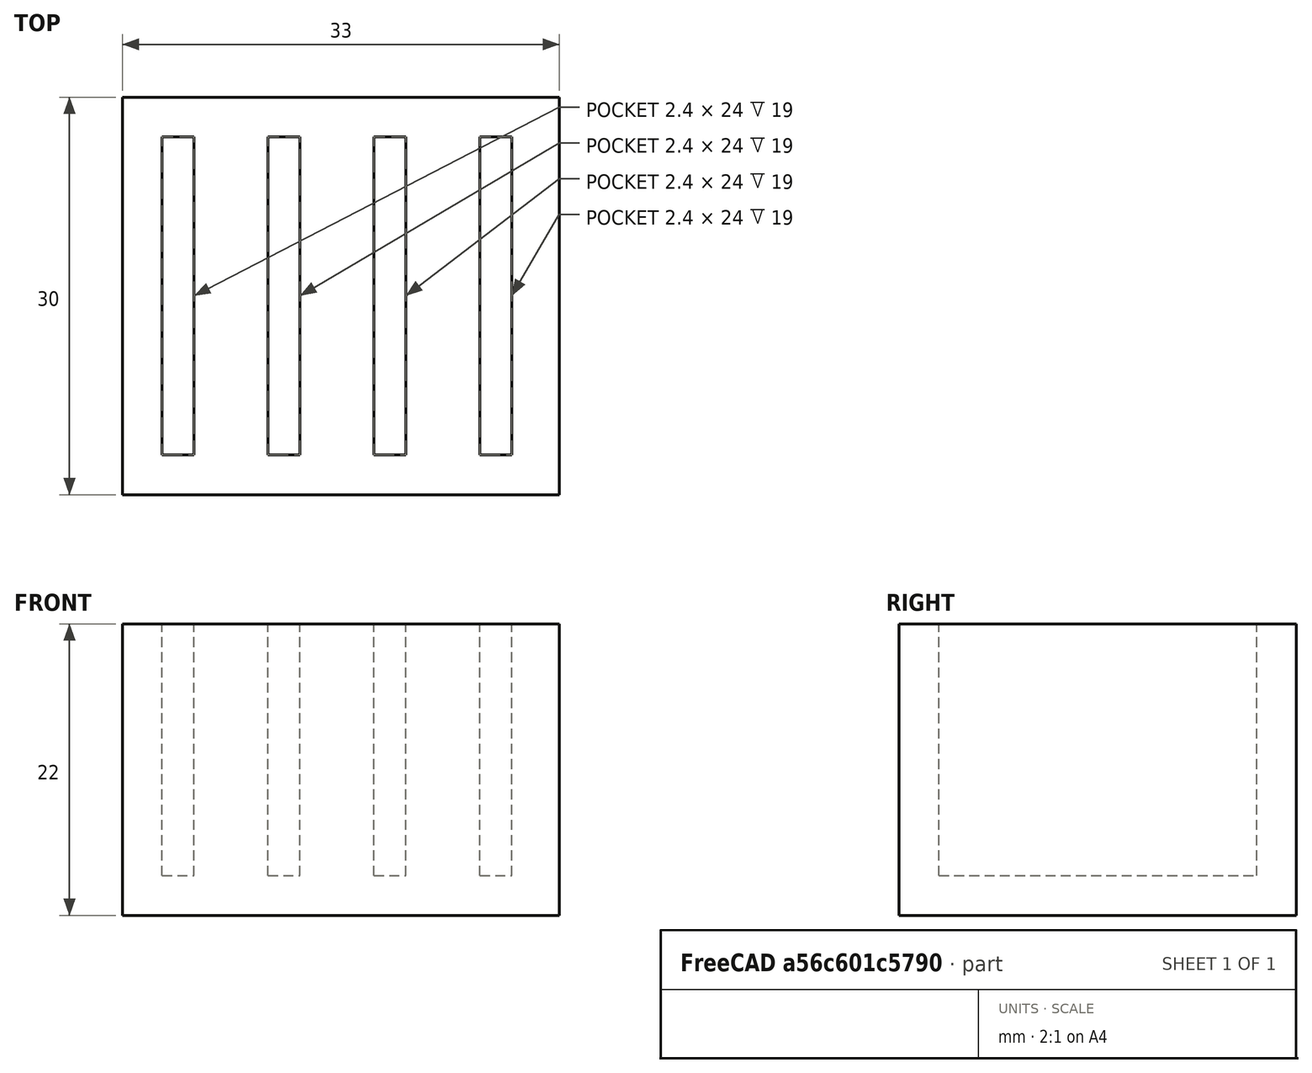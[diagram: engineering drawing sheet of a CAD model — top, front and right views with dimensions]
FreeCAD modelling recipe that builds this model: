
FCSTD DOCUMENT  (FreeCAD 1.0R39285 (Git))
Label: ojt1_t08r01_sd_holder
License: All rights reserved
objects: Part::Box×5, Part::MultiFuse×1, Part::Cut×1
note: 7 computed .brp shape members not serialized (recipe doc carries the construction recipe); baked Part::Feature solids carry a one-line shape summary decoded from their .brp

FEATURE [Part::Box] Box  label="slot"
  AttacherType = Attacher::AttachEngine3D
  Height = 22
  Length = 2.4
  Width = 24
FEATURE [Part::Box] Box001  label="slot001"
  AttacherType = Attacher::AttachEngine3D
  Height = 22
  Length = 2.4
  Placement = pos=(8,0,0) rot=(0,0,1;0rad)
  Width = 24
FEATURE [Part::Box] Box002  label="slot002"
  AttacherType = Attacher::AttachEngine3D
  Height = 22
  Length = 2.4
  Placement = pos=(16,0,0) rot=(0,0,1;0rad)
  Width = 24
FEATURE [Part::Box] Box003  label="slot003"
  AttacherType = Attacher::AttachEngine3D
  Height = 22
  Length = 2.4
  Placement = pos=(24,0,0) rot=(0,0,1;0rad)
  Width = 24
FEATURE [Part::MultiFuse] Fusion  label="slots"
  Refine = true
  Shapes = -> [Box003,Box,Box001,Box002]
FEATURE [Part::Box] Box004  label="basis"
  AttacherType = Attacher::AttachEngine3D
  Height = 22
  Length = 33
  Placement = pos=(-3,-3,-3) rot=(0,0,1;0rad)
  Width = 30
FEATURE [Part::Cut] Cut  label="sd_holder"
  Base = -> Box004
  Placement = pos=(3,3,3) rot=(0,0,1;0rad)
  Refine = true
  Tool = -> Fusion
